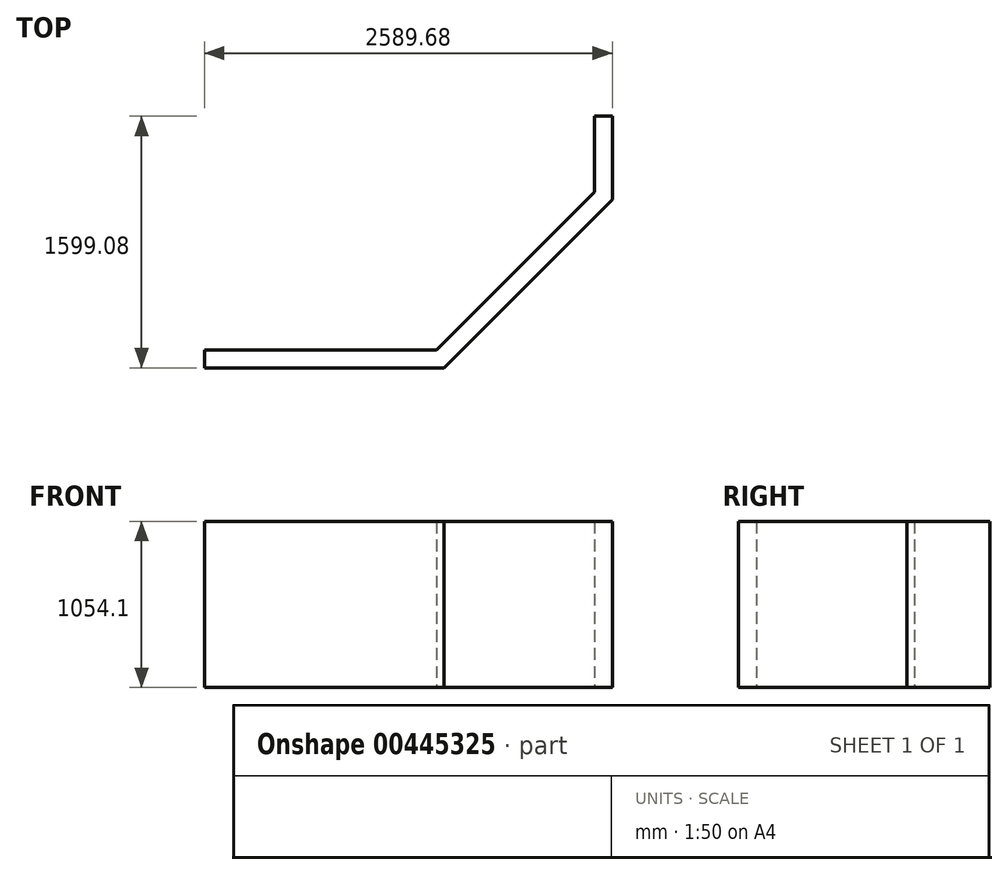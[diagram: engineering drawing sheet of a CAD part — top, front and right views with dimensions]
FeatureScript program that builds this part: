
annotation { "Feature Type Name" : "Feature", "Feature Type Description" : "" }
export const myFeature = defineFeature(function(context is Context, id is Id, definition is map)
    precondition{}
    {
        {
            var Q0;
            Q0=qCreatedBy(makeId("Top.planeOp"),FACE);
            var sketch = newSketch(context, id + "F0", { "sketchPlane" : qUnion([Q0])});
            skLineSegment(sketch, "E0", {"start": v(0, 0) * mm, "end": v(1471.7, 0) * mm});
            skLineSegment(sketch, "E1", {"start": v(1471.7, 0) * mm, "end": v(2475.38, 1003.67) * mm});
            skLineSegment(sketch, "E2", {"start": v(2475.38, 1003.67) * mm, "end": v(2475.38, 1484.78) * mm});
            skLineSegment(sketch, "E3", {"start": v(2475.38, 1484.78) * mm, "end": v(2589.68, 1484.78) * mm});
            skLineSegment(sketch, "E4", {"start": v(2589.68, 1484.78) * mm, "end": v(2589.68, 956.33) * mm});
            skLineSegment(sketch, "E5", {"start": v(2589.68, 956.33) * mm, "end": v(1519.05, -114.3) * mm});
            skLineSegment(sketch, "E6", {"start": v(1519.05, -114.3) * mm, "end": v(0, -114.3) * mm});
            skLineSegment(sketch, "E7", {"start": v(0, -114.3) * mm, "end": v(0, 0) * mm});
            skSolve(sketch);
        }
        {
            var Q0;
            Q0=makeQuery(id+"F0.imprint","IMPRINT",FACE,{"disambiguationData":[TD([[makeQuery(id+"F0.imprint","IMPRINT",EDGE,{"derivedFrom":sQuery(id+"F0.wireOp",EDGE,"E0")}),-1.0]])]});
            extrude(context, id + "F1", {"entities" : qUnion([Q0]), "depth" : 1054.1 * mm});
        }
    });
